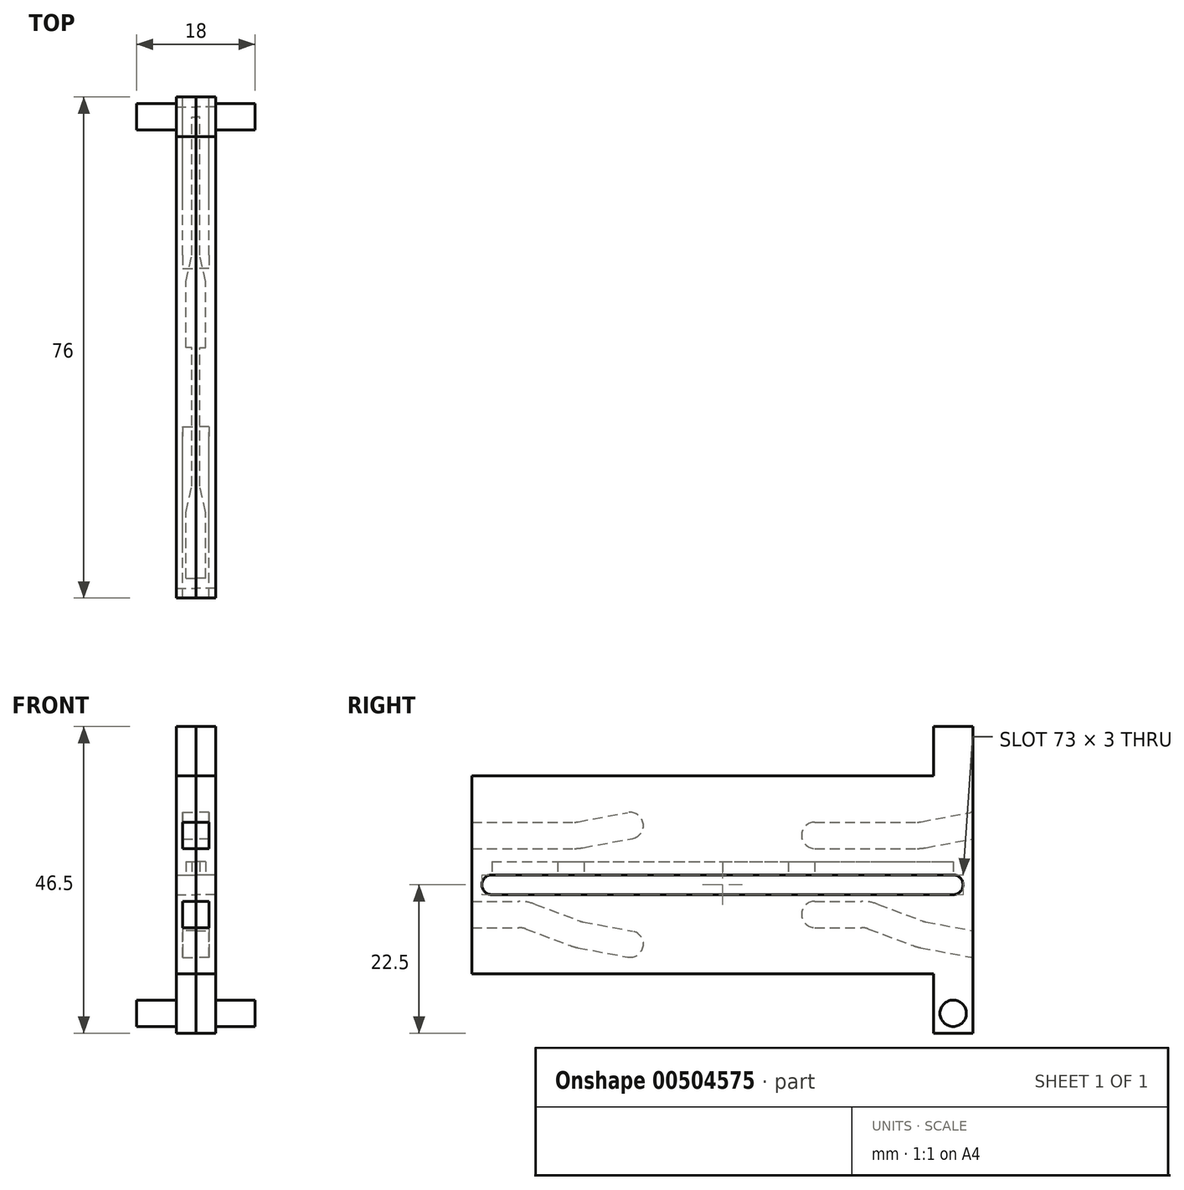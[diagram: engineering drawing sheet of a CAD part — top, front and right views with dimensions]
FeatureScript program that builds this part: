
annotation { "Feature Type Name" : "Feature", "Feature Type Description" : "" }
export const myFeature = defineFeature(function(context is Context, id is Id, definition is map)
    precondition{}
    {
        {
            var Q0;
            Q0=qCreatedBy(makeId("Front.planeOp"),FACE);
            var sketch = newSketch(context, id + "F0", { "sketchPlane" : qUnion([Q0])});
            skLineSegment(sketch, "E0.bottom", {"start": v(1.5, -15) * mm, "end": v(-1.5, -15) * mm});
            skLineSegment(sketch, "E0.top", {"start": v(1.5, 15) * mm, "end": v(-1.5, 15) * mm});
            skLineSegment(sketch, "E0.left", {"start": v(1.5, -15) * mm, "end": v(1.5, 15) * mm});
            skLineSegment(sketch, "E0.right", {"start": v(-1.5, -15) * mm, "end": v(-1.5, 15) * mm});
            skPoint(sketch, "E0.middle", {"position": v(0, 0) * mm});
            skSolve(sketch);
        }
        {
            var Q0;
            Q0=makeQuery(id+"F0.imprint","IMPRINT",FACE,{"disambiguationData":[TD([[makeQuery(id+"F0.imprint","IMPRINT",EDGE,{"derivedFrom":sQuery(id+"F0.wireOp",EDGE,"E0.bottom")}),-1.0]])]});
            var Q1;
            Q1 = qSketchRegion(id + "F2", true);
            extrude(context, id + "F1", {"entities" : qUnion([Q0, Q1]), "depth" : 76 * mm});
        }
        {
            var Q0;
            Q0=makeQuery(id+"F1.opExtrude","SWEPT_FACE",FACE,{"disambiguationData":[OSD([sQuery(id+"F0.wireOp",EDGE,"E0.left")])]});
            var sketch = newSketch(context, id + "F2", { "sketchPlane" : qUnion([Q0])});
            skLineSegment(sketch, "E1", {"start": v(-76, 6) * mm, "end": v(-68, 6) * mm});
            skLineSegment(sketch, "E2", {"start": v(-76, 0) * mm, "end": v(0, 0) * mm, "construction": true});
            skPoint(sketch, "E3.visualSharp", {"position": v(-68, 6) * mm});
            skLineSegment(sketch, "E4.MirrorCS", {"start": v(-76, -6) * mm, "end": v(-68.9, -6) * mm});
            skLineSegment(sketch, "E5", {"start": v(-68, 6) * mm, "end": v(-60.46, 6) * mm});
            skLineSegment(sketch, "E6", {"start": v(-67.15, -6.32) * mm, "end": v(-60.4, -8.85) * mm});
            skLineSegment(sketch, "E7", {"start": v(-59.54, 6.09) * mm, "end": v(-52, 7.5) * mm});
            skLineSegment(sketch, "E8", {"start": v(-59.57, -9.08) * mm, "end": v(-52, -10.5) * mm});
            skCircle(sketch, "E9", {"center": v(-52, 7.5) * mm, "radius": 2 * mm});
            skCircle(sketch, "E10", {"center": v(-52, -10.5) * mm, "radius": 2 * mm});
            skPoint(sketch, "E11.visualSharp", {"position": v(-68, -6) * mm});
            skArc(sketch, "E11.filletArc", {"start": v(-67.15, -6.32) * mm, "mid": v(-68.01, -6.08) * mm, "end": v(-68.9, -6) * mm});
            skPoint(sketch, "E12.visualSharp", {"position": v(-60, 6) * mm});
            skArc(sketch, "E12.filletArc", {"start": v(-60.46, 6) * mm, "mid": v(-60, 6.02) * mm, "end": v(-59.54, 6.09) * mm});
            skLineSegment(sketch, "E13.1.0.0", {"start": v(-7.54, 6.09) * mm, "end": v(0, 7.5) * mm});
            skLineSegment(sketch, "E13.1.0.1", {"start": v(-15.15, -6.32) * mm, "end": v(-8.4, -8.85) * mm});
            skPoint(sketch, "E13.1.0.2", {"position": v(-16, 6) * mm});
            skPoint(sketch, "E13.1.0.3", {"position": v(-16, -6) * mm});
            skLineSegment(sketch, "E13.1.0.4", {"start": v(-24, -6) * mm, "end": v(-16.9, -6) * mm});
            skLineSegment(sketch, "E13.1.0.5", {"start": v(-24, 6) * mm, "end": v(-16, 6) * mm});
            skPoint(sketch, "E13.1.0.6", {"position": v(-8, 6) * mm});
            skLineSegment(sketch, "E13.1.0.7", {"start": v(-7.57, -9.08) * mm, "end": v(0, -10.5) * mm});
            skLineSegment(sketch, "E13.1.0.8", {"start": v(-16, 6) * mm, "end": v(-8.46, 6) * mm});
            skArc(sketch, "E13.1.0.9", {"start": v(-15.15, -6.32) * mm, "mid": v(-16.01, -6.08) * mm, "end": v(-16.9, -6) * mm});
            skArc(sketch, "E13.1.0.10", {"start": v(-8.46, 6) * mm, "mid": v(-8, 6.02) * mm, "end": v(-7.54, 6.09) * mm});
            skLineSegment(sketch, "E13.direction1", {"start": v(-76, -6) * mm, "end": v(-24, -6) * mm, "construction": true});
            skCircle(sketch, "E14", {"center": v(0, 7.5) * mm, "radius": 2 * mm});
            skCircle(sketch, "E15", {"center": v(0, -10.5) * mm, "radius": 2 * mm});
            skCircle(sketch, "E16", {"center": v(-24, 6) * mm, "radius": 2 * mm});
            skCircle(sketch, "E17", {"center": v(-24, -6) * mm, "radius": 2 * mm});
            skLineSegment(sketch, "E18", {"start": v(-38, 15) * mm, "end": v(-38, -15.73) * mm, "construction": true});
            skLineSegment(sketch, "E19", {"start": v(-73, 0) * mm, "end": v(-38, 0) * mm});
            skLineSegment(sketch, "E20", {"start": v(-73, -3) * mm, "end": v(-38, -3) * mm});
            skLineSegment(sketch, "E21", {"start": v(-38, -3) * mm, "end": v(-38, 0) * mm});
            skArc(sketch, "E22", {"start": v(-73, 0) * mm, "mid": v(-74.5, -1.5) * mm, "end": v(-73, -3) * mm});
            skLineSegment(sketch, "E23.MirrorCS", {"start": v(-3, 0) * mm, "end": v(-38, 0) * mm});
            skLineSegment(sketch, "E24.MirrorCS", {"start": v(-3, -3) * mm, "end": v(-38, -3) * mm});
            skArc(sketch, "E25.MirrorCS", {"start": v(-3, 0) * mm, "mid": v(-1.5, -1.5) * mm, "end": v(-3, -3) * mm});
            skPoint(sketch, "E26.visualSharp", {"position": v(-60, -9) * mm});
            skArc(sketch, "E26.filletArc", {"start": v(-60.4, -8.85) * mm, "mid": v(-60, -8.98) * mm, "end": v(-59.57, -9.08) * mm});
            skPoint(sketch, "E27.visualSharp", {"position": v(-8, -9) * mm});
            skArc(sketch, "E27.filletArc", {"start": v(-8.4, -8.85) * mm, "mid": v(-8, -8.98) * mm, "end": v(-7.57, -9.08) * mm});
            skSolve(sketch);
        }
        {
            var Q0;
            Q0=makeQuery(id+"F1.opExtrude","CAP_FACE",FACE,{"disambiguationData":[OSD([sQuery(id+"F0.wireOp",EDGE,"E0.bottom"),sQuery(id+"F0.wireOp",EDGE,"E0.top"),sQuery(id+"F0.wireOp",EDGE,"E0.left"),sQuery(id+"F0.wireOp",EDGE,"E0.right")])],"isStart":false});
            var sketch = newSketch(context, id + "F3", { "sketchPlane" : qUnion([Q0])});
            skLineSegment(sketch, "E28.bottom", {"start": v(1.5, 8) * mm, "end": v(-0.5, 8) * mm});
            skLineSegment(sketch, "E28.top", {"start": v(1.5, 0) * mm, "end": v(-0.5, 0) * mm});
            skLineSegment(sketch, "E28.left", {"start": v(1.5, 8) * mm, "end": v(1.5, 0) * mm});
            skLineSegment(sketch, "E28.right", {"start": v(-0.5, 8) * mm, "end": v(-0.5, 0) * mm});
            skLineSegment(sketch, "E29.MirrorCS", {"start": v(-0.5, -8) * mm, "end": v(-0.5, 0) * mm});
            skLineSegment(sketch, "E30.MirrorCS", {"start": v(1.5, -8) * mm, "end": v(1.5, 0) * mm});
            skLineSegment(sketch, "E31.MirrorCS", {"start": v(1.5, -8) * mm, "end": v(-0.5, -8) * mm});
            skLineSegment(sketch, "E32", {"start": v(1.5, 4) * mm, "end": v(-0.5, 4) * mm});
            skLineSegment(sketch, "E33.MirrorCS", {"start": v(1.5, -4) * mm, "end": v(-0.5, -4) * mm});
            skSolve(sketch);
        }
        {
            var Q0;
            {var subQ0=sQuery(id+"F3.wireOp",EDGE,"E31.MirrorCS");Q0=makeQuery(id+"F3.imprint","IMPRINT",FACE,{"disambiguationData":[TD([[makeQuery(id+"F3.imprint","IMPRINT",EDGE,{"derivedFrom":subQ0}),-1.0]])]});}
            var Q1;
            Q1=sQuery(id+"F2.wireOp",EDGE,"E4.MirrorCS");
            var Q2;
            Q2=sQuery(id+"F2.wireOp",EDGE,"E6");
            var Q3;
            Q3=sQuery(id+"F2.wireOp",EDGE,"E8");
            var Q4;
            Q4=sQuery(id+"F2.wireOp",EDGE,"E11.filletArc");
            var Q5;
            Q5=sQuery(id+"F2.wireOp",EDGE,"E26.filletArc");
            sweep(context, id + "F4", {"operationType" : NewBodyOperationType.REMOVE, "profiles" : qUnion([Q0]), "path" : qUnion([Q1, Q2, Q3, Q4, Q5])});
        }
        {
            var Q0;
            Q0=makeQuery(id+"F3.imprint","IMPRINT",FACE,{"disambiguationData":[TD([[makeQuery(id+"F3.imprint","IMPRINT",EDGE,{"derivedFrom":sQuery(id+"F3.wireOp",EDGE,"E28.bottom")}),1.0]])]});
            var Q1;
            Q1=sQuery(id+"F2.wireOp",EDGE,"E1");
            var Q2;
            Q2=sQuery(id+"F2.wireOp",EDGE,"E5");
            var Q3;
            Q3=sQuery(id+"F2.wireOp",EDGE,"E7");
            var Q4;
            Q4=sQuery(id+"F2.wireOp",EDGE,"E12.filletArc");
            sweep(context, id + "F5", {"operationType" : NewBodyOperationType.REMOVE, "profiles" : qUnion([Q0]), "path" : qUnion([Q1, Q2, Q3, Q4])});
        }
        {
            var Q0;
            {var subQ1=sQuery(id+"F3.wireOp",EDGE,"E28.bottom");Q0=makeQuery(id+"F3.imprint","IMPRINT",FACE,{"disambiguationData":[TD([[makeQuery(id+"F3.imprint","IMPRINT",EDGE,{"derivedFrom":subQ1}),-1.0]])]});}
            cPlane(context, id + "F6", {"entities" : qUnion([Q0]), "cplaneType" : CPlaneType.OFFSET, "offset" : 52 * mm, "oppositeDirection" : true, "width" : 150 * mm, "height" : 150 * mm});
        }
        {
            var Q0;
            Q0=qCreatedBy(id+"F6.planeOp",FACE);
            var sketch = newSketch(context, id + "F7", { "sketchPlane" : qUnion([Q0])});
            skLineSegment(sketch, "E34.bottom", {"start": v(-0.5, 0) * mm, "end": v(1.5, 0) * mm});
            skLineSegment(sketch, "E34.top", {"start": v(-0.5, -8) * mm, "end": v(1.5, -8) * mm});
            skLineSegment(sketch, "E34.left", {"start": v(-0.5, 0) * mm, "end": v(-0.5, -8) * mm});
            skLineSegment(sketch, "E34.right", {"start": v(1.5, 0) * mm, "end": v(1.5, -8) * mm});
            skLineSegment(sketch, "E35.bottom", {"start": v(1.5, 8) * mm, "end": v(-0.5, 8) * mm});
            skLineSegment(sketch, "E35.top", {"start": v(1.5, 0) * mm, "end": v(-0.5, 0) * mm});
            skLineSegment(sketch, "E35.left", {"start": v(1.5, 8) * mm, "end": v(1.5, 0) * mm});
            skLineSegment(sketch, "E35.right", {"start": v(-0.5, 8) * mm, "end": v(-0.5, 0) * mm});
            skLineSegment(sketch, "E36", {"start": v(1.5, 4) * mm, "end": v(-0.5, 4) * mm});
            skLineSegment(sketch, "E37", {"start": v(1.5, -4) * mm, "end": v(-0.5, -4) * mm});
            skSolve(sketch);
        }
        {
            var Q0;
            Q0=makeQuery(id+"F7.imprint","IMPRINT",FACE,{"disambiguationData":[TD([[makeQuery(id+"F7.imprint","IMPRINT",EDGE,{"derivedFrom":sQuery(id+"F7.wireOp",EDGE,"E34.top")}),1.0]])]});
            var Q1;
            Q1=sQuery(id+"F2.wireOp",EDGE,"E13.1.0.4");
            var Q2;
            Q2=sQuery(id+"F2.wireOp",EDGE,"E13.1.0.1");
            var Q3;
            Q3=sQuery(id+"F2.wireOp",EDGE,"E13.1.0.9");
            var Q4;
            Q4=sQuery(id+"F2.wireOp",EDGE,"E13.1.0.7");
            var Q5;
            Q5=sQuery(id+"F2.wireOp",EDGE,"E27.filletArc");
            sweep(context, id + "F8", {"operationType" : NewBodyOperationType.REMOVE, "profiles" : qUnion([Q0]), "path" : qUnion([Q1, Q2, Q3, Q4, Q5])});
        }
        {
            var Q0;
            Q0=makeQuery(id+"F7.imprint","IMPRINT",FACE,{"disambiguationData":[TD([[makeQuery(id+"F7.imprint","IMPRINT",EDGE,{"derivedFrom":sQuery(id+"F7.wireOp",EDGE,"E35.bottom")}),1.0]])]});
            var Q1;
            Q1=sQuery(id+"F2.wireOp",EDGE,"E13.1.0.5");
            var Q2;
            Q2=sQuery(id+"F2.wireOp",EDGE,"E13.1.0.8");
            var Q3;
            Q3=sQuery(id+"F2.wireOp",EDGE,"E13.1.0.10");
            var Q4;
            Q4=sQuery(id+"F2.wireOp",EDGE,"E13.1.0.0");
            sweep(context, id + "F9", {"operationType" : NewBodyOperationType.REMOVE, "profiles" : qUnion([Q0]), "path" : qUnion([Q1, Q2, Q3, Q4])});
        }
        {
            var Q0;
            Q0=makeQuery(id+"F2.imprint","IMPRINT",FACE,{"disambiguationData":[TD([[makeQuery(id+"F2.imprint","IMPRINT",EDGE,{"derivedFrom":sQuery(id+"F2.wireOp",EDGE,"E9")}),1.0]])]});
            var Q1;
            Q1=makeQuery(id+"F2.imprint","IMPRINT",FACE,{"disambiguationData":[TD([[makeQuery(id+"F2.imprint","IMPRINT",EDGE,{"derivedFrom":sQuery(id+"F2.wireOp",EDGE,"E10")}),1.0]])]});
            var Q2;
            {var subQ0=sQuery(id+"F2.wireOp",EDGE,"E13.1.0.0");var subQ1=makeQuery(id+"F1.opExtrude","CAP_EDGE",EDGE,{"disambiguationData":[OSD([sQuery(id+"F0.wireOp",EDGE,"E0.left")])],"isStart":true});var subQ2=makeQuery(id+"F2.imprint","INTERSECT",VERTEX,{"derivedFrom":[subQ1,subQ0]});Q2=makeQuery(id+"F2.imprint","IMPRINT",FACE,{"disambiguationData":[TD([[makeQuery(id+"F2.imprint","IMPRINT",EDGE,{"disambiguationData":[TD([[subQ2,1.0]])],"derivedFrom":subQ0}),1.0]])]});}
            var Q3;
            {var subQ0=sQuery(id+"F2.wireOp",EDGE,"E13.1.0.7");var subQ1=makeQuery(id+"F1.opExtrude","CAP_EDGE",EDGE,{"disambiguationData":[OSD([sQuery(id+"F0.wireOp",EDGE,"E0.left")])],"isStart":true});var subQ2=makeQuery(id+"F2.imprint","INTERSECT",VERTEX,{"derivedFrom":[subQ1,subQ0]});Q3=makeQuery(id+"F2.imprint","IMPRINT",FACE,{"disambiguationData":[TD([[makeQuery(id+"F2.imprint","IMPRINT",EDGE,{"disambiguationData":[TD([[subQ2,1.0]])],"derivedFrom":subQ0}),-1.0]])]});}
            var Q4;
            {var subQ0=sQuery(id+"F2.wireOp",EDGE,"E16");var subQ1=makeQuery(id+"F2.imprint","INTERSECT",VERTEX,{"derivedFrom":[sQuery(id+"F2.wireOp",EDGE,"E13.1.0.5"),subQ0]});Q4=makeQuery(id+"F2.imprint","IMPRINT",FACE,{"disambiguationData":[TD([[makeQuery(id+"F2.imprint","IMPRINT",EDGE,{"disambiguationData":[TD([[subQ1,-1.0]])],"derivedFrom":subQ0}),1.0]])]});}
            var Q5;
            {var subQ0=sQuery(id+"F2.wireOp",EDGE,"E17");var subQ1=makeQuery(id+"F2.imprint","INTERSECT",VERTEX,{"derivedFrom":[sQuery(id+"F2.wireOp",EDGE,"E13.1.0.4"),subQ0]});Q5=makeQuery(id+"F2.imprint","IMPRINT",FACE,{"disambiguationData":[TD([[makeQuery(id+"F2.imprint","IMPRINT",EDGE,{"disambiguationData":[TD([[subQ1,-1.0]])],"derivedFrom":subQ0}),1.0]])]});}
            var Q6;
            Q6=makeQuery(id+"F2.imprint","IMPRINT",FACE,{"disambiguationData":[TD([[makeQuery(id+"F2.imprint","IMPRINT",EDGE,{"derivedFrom":sQuery(id+"F2.wireOp",EDGE,"E17")}),1.0]])]});
            var Q7;
            Q7=makeQuery(id+"F2.imprint","IMPRINT",FACE,{"disambiguationData":[TD([[makeQuery(id+"F2.imprint","IMPRINT",EDGE,{"derivedFrom":sQuery(id+"F2.wireOp",EDGE,"E16")}),1.0]])]});
            extrude(context, id + "F10", {"entities" : qUnion([Q0, Q1, Q2, Q3, Q4, Q5, Q6, Q7]), "operationType" : NewBodyOperationType.REMOVE, "oppositeDirection" : true, "depth" : 2 * mm});
        }
        {
            var Q0;
            Q0=makeQuery(id+"F2.imprint","IMPRINT",FACE,{"disambiguationData":[TD([[makeQuery(id+"F2.imprint","IMPRINT",EDGE,{"derivedFrom":sQuery(id+"F2.wireOp",EDGE,"E19")}),-1.0]])]});
            var Q1;
            Q1=makeQuery(id+"F2.imprint","IMPRINT",FACE,{"disambiguationData":[TD([[makeQuery(id+"F2.imprint","IMPRINT",EDGE,{"derivedFrom":sQuery(id+"F2.wireOp",EDGE,"E21")}),-1.0]])]});
            extrude(context, id + "F11", {"entities" : qUnion([Q0, Q1]), "operationType" : NewBodyOperationType.REMOVE, "endBound" : BoundingType.THROUGH_ALL, "oppositeDirection" : true, "depth" : 25 * mm});
        }
        {
            var Q0;
            Q0=makeQuery(id+"F11.boolean.opBoolean","COPY",FACE,{"derivedFrom":makeQuery(id+"F11.opExtrude","SWEPT_FACE",FACE,{"disambiguationData":[OSD([sQuery(id+"F2.wireOp",EDGE,"E19"),sQuery(id+"F2.wireOp",EDGE,"E23.MirrorCS")])]})});
            var sketch = newSketch(context, id + "F12", { "sketchPlane" : qUnion([Q0])});
            skLineSegment(sketch, "E38", {"start": v(1.5, 73) * mm, "end": v(0, 73) * mm});
            skLineSegment(sketch, "E39", {"start": v(0, 73) * mm, "end": v(0, 63) * mm});
            skLineSegment(sketch, "E40", {"start": v(0, 63) * mm, "end": v(0.9, 59) * mm});
            skLineSegment(sketch, "E41", {"start": v(0.9, 59) * mm, "end": v(0.9, 38) * mm});
            skLineSegment(sketch, "E42", {"start": v(0.9, 38) * mm, "end": v(1.5, 38) * mm});
            skLineSegment(sketch, "E43", {"start": v(1.5, 38) * mm, "end": v(1.5, 73) * mm});
            skLineSegment(sketch, "E44.0.1.0", {"start": v(1.5, 3) * mm, "end": v(1.5, 38) * mm});
            skLineSegment(sketch, "E44.0.1.1", {"start": v(0, 28) * mm, "end": v(0.9, 24) * mm});
            skLineSegment(sketch, "E44.0.1.2", {"start": v(1.5, 38) * mm, "end": v(0, 38) * mm});
            skLineSegment(sketch, "E44.0.1.3", {"start": v(0, 38) * mm, "end": v(0, 28) * mm});
            skLineSegment(sketch, "E44.0.1.4", {"start": v(0.9, 24) * mm, "end": v(0.9, 3) * mm});
            skLineSegment(sketch, "E44.0.1.5", {"start": v(0.9, 3) * mm, "end": v(1.5, 3) * mm});
            skLineSegment(sketch, "E44.direction1", {"start": v(0.9, 38) * mm, "end": v(25.9, 38) * mm, "construction": true});
            skLineSegment(sketch, "E44.direction2", {"start": v(0.9, 38) * mm, "end": v(0.9, 3) * mm, "construction": true});
            skSolve(sketch);
        }
        {
            var Q0;
            Q0=makeQuery(id+"F12.imprint","IMPRINT",FACE,{"disambiguationData":[TD([[makeQuery(id+"F12.imprint","IMPRINT",EDGE,{"derivedFrom":sQuery(id+"F12.wireOp",EDGE,"E38")}),-1.0]])]});
            var Q1;
            {var subQ3=sQuery(id+"F12.wireOp",EDGE,"E44.0.1.0");Q1=makeQuery(id+"F12.imprint","IMPRINT",FACE,{"disambiguationData":[TD([[makeQuery(id+"F12.imprint","IMPRINT",EDGE,{"derivedFrom":subQ3}),-1.0]])]});}
            extrude(context, id + "F13", {"entities" : qUnion([Q0, Q1]), "operationType" : NewBodyOperationType.REMOVE, "oppositeDirection" : true, "depth" : 2 * mm});
        }
        {
            var Q0;
            Q0=makeQuery(id+"F1.opExtrude","SWEPT_FACE",FACE,{"disambiguationData":[OSD([sQuery(id+"F0.wireOp",EDGE,"E0.top")])]});
            var sketch = newSketch(context, id + "F14", { "sketchPlane" : qUnion([Q0])});
            skLineSegment(sketch, "E45.bottom", {"start": v(1.5, 0) * mm, "end": v(-1.5, 0) * mm});
            skLineSegment(sketch, "E45.top", {"start": v(1.5, -6) * mm, "end": v(-1.5, -6) * mm});
            skLineSegment(sketch, "E45.left", {"start": v(1.5, 0) * mm, "end": v(1.5, -6) * mm});
            skLineSegment(sketch, "E45.right", {"start": v(-1.5, 0) * mm, "end": v(-1.5, -6) * mm});
            skSolve(sketch);
        }
        {
            var Q0;
            Q0=makeQuery(id+"F14.imprint","IMPRINT",FACE,{"disambiguationData":[TD([[makeQuery(id+"F14.imprint","IMPRINT",EDGE,{"derivedFrom":sQuery(id+"F14.wireOp",EDGE,"E45.bottom")}),1.0]])]});
            extrude(context, id + "F15", {"entities" : qUnion([Q0]), "operationType" : NewBodyOperationType.ADD, "depth" : 7.5 * mm, "offsetDistance" : 25 * mm});
        }
        {
            var Q0;
            Q0=makeQuery(id+"F1.opExtrude","SWEPT_FACE",FACE,{"disambiguationData":[OSD([sQuery(id+"F0.wireOp",EDGE,"E0.bottom")])]});
            var sketch = newSketch(context, id + "F16", { "sketchPlane" : qUnion([Q0])});
            skLineSegment(sketch, "E46.bottom", {"start": v(-1.5, 0) * mm, "end": v(1.5, 0) * mm});
            skLineSegment(sketch, "E46.top", {"start": v(-1.5, 6) * mm, "end": v(1.5, 6) * mm});
            skLineSegment(sketch, "E46.left", {"start": v(-1.5, 0) * mm, "end": v(-1.5, 6) * mm});
            skLineSegment(sketch, "E46.right", {"start": v(1.5, 0) * mm, "end": v(1.5, 6) * mm});
            skSolve(sketch);
        }
        {
            var Q0;
            Q0=makeQuery(id+"F16.imprint","IMPRINT",FACE,{"disambiguationData":[TD([[makeQuery(id+"F16.imprint","IMPRINT",EDGE,{"derivedFrom":sQuery(id+"F16.wireOp",EDGE,"E46.bottom")}),-1.0]])]});
            extrude(context, id + "F17", {"entities" : qUnion([Q0]), "operationType" : NewBodyOperationType.ADD, "depth" : 9 * mm, "offsetDistance" : 25 * mm});
        }
        {
            var Q0;
            Q0=makeQuery(id+"F17.boolean.opBoolean","MERGE",FACE,{"derivedFrom":[makeQuery(id+"F15.boolean.opBoolean","MERGE",FACE,{"derivedFrom":[makeQuery(id+"F1.opExtrude","SWEPT_FACE",FACE,{"disambiguationData":[OSD([sQuery(id+"F0.wireOp",EDGE,"E0.right")])]}),makeQuery(id+"F15.opExtrude","SWEPT_FACE",FACE,{"disambiguationData":[OSD([sQuery(id+"F14.wireOp",EDGE,"E45.right")])]})]}),makeQuery(id+"F17.opExtrude","SWEPT_FACE",FACE,{"disambiguationData":[OSD([sQuery(id+"F16.wireOp",EDGE,"E46.left")])]})]});
            var sketch = newSketch(context, id + "F18", { "sketchPlane" : qUnion([Q0])});
            skCircle(sketch, "E47", {"center": v(3, -21) * mm, "radius": 2 * mm});
            skPoint(sketch, "E47.centerSnap0", {"position": v(3, -24) * mm});
            skSolve(sketch);
        }
        {
            var Q0;
            Q0=makeQuery(id+"F18.imprint","IMPRINT",FACE,{"disambiguationData":[TD([[makeQuery(id+"F18.imprint","IMPRINT",EDGE,{"derivedFrom":sQuery(id+"F18.wireOp",EDGE,"E47")}),1.0]])]});
            extrude(context, id + "F19", {"entities" : qUnion([Q0]), "operationType" : NewBodyOperationType.ADD, "depth" : 6 * mm, "offsetDistance" : 25 * mm});
        }
        {
            var Q0;
            Q0=makeQuery(id+"F1.opExtrude","SWEPT_BODY",BODY,{"disambiguationData":[OSD([sQuery(id+"F0.wireOp",EDGE,"E0.bottom"),sQuery(id+"F0.wireOp",EDGE,"E0.top"),sQuery(id+"F0.wireOp",EDGE,"E0.left"),sQuery(id+"F0.wireOp",EDGE,"E0.right")])]});
            var Q1;
            {var subQ8=sQuery(id+"F0.wireOp",EDGE,"E0.bottom");var subQ15=sQuery(id+"F0.wireOp",EDGE,"E0.left");Q1=makeQuery(id+"F9.boolean.opBoolean","SPLIT",FACE,{"disambiguationData":[TD([makeQuery(id+"F1.opExtrude","SWEPT_FACE",FACE,{"disambiguationData":[OSD([subQ8])]})])],"derivedFrom":makeQuery(id+"F1.opExtrude","SWEPT_FACE",FACE,{"disambiguationData":[OSD([subQ15])]})});}
            mirror(context, id + "F20", {"entities" : qUnion([Q0]), "mirrorPlane" : qUnion([Q1])});
        }
    });
